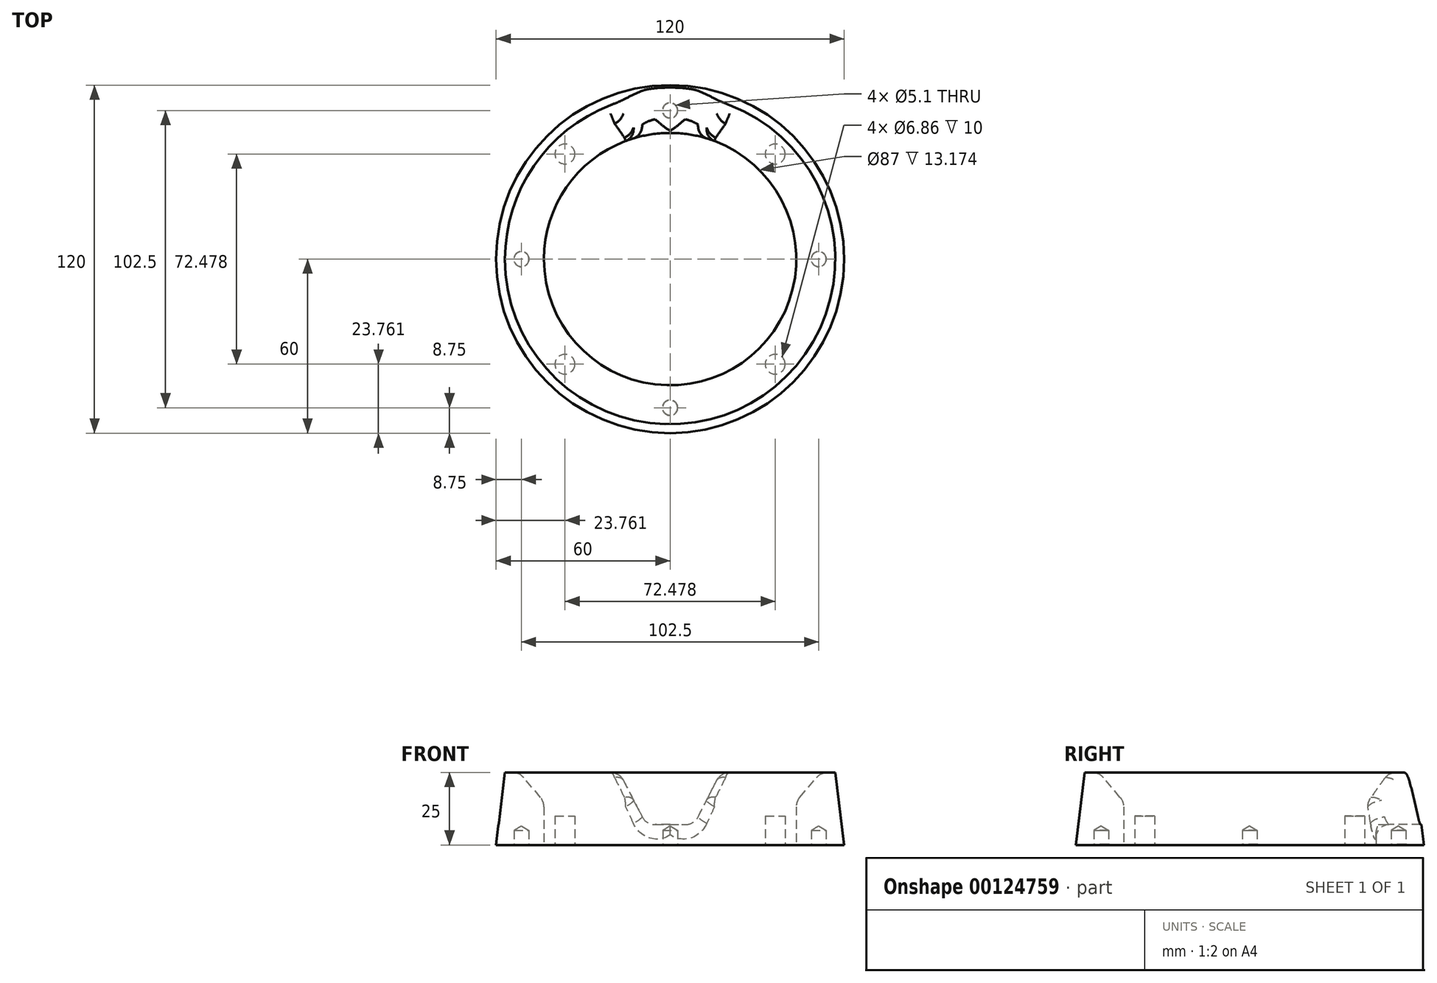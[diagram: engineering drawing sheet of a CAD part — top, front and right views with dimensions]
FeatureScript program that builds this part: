
annotation { "Feature Type Name" : "Feature", "Feature Type Description" : "" }
export const myFeature = defineFeature(function(context is Context, id is Id, definition is map)
    precondition{}
    {
        {
            var Q0;
            Q0=qCreatedBy(makeId("Front.planeOp"),FACE);
            var sketch = newSketch(context, id + "F0", { "sketchPlane" : qUnion([Q0])});
            skLineSegment(sketch, "E0", {"start": v(60, 0) * mm, "end": v(56.93, 25) * mm});
            skLineSegment(sketch, "E1", {"start": v(56.93, 25) * mm, "end": v(51.93, 25) * mm});
            skLineSegment(sketch, "E2", {"start": v(43.5, 0) * mm, "end": v(60, 0) * mm});
            skLineSegment(sketch, "E3", {"start": v(51.93, 25) * mm, "end": v(43.5, 15) * mm});
            skLineSegment(sketch, "E4", {"start": v(43.5, 15) * mm, "end": v(43.5, 0) * mm});
            skLineSegment(sketch, "E5", {"start": v(0, 0) * mm, "end": v(0, 25) * mm, "construction": true});
            skSolve(sketch);
        }
        {
            var Q0;
            Q0=makeQuery(id+"F0.imprint","IMPRINT",FACE,{"disambiguationData":[TD([[makeQuery(id+"F0.imprint","IMPRINT",EDGE,{"derivedFrom":sQuery(id+"F0.wireOp",EDGE,"E0")}),1.0]])]});
            var Q1;
            Q1=sQuery(id+"F0.wireOp",EDGE,"E5");
            revolve(context, id + "F1", {"entities" : qUnion([Q0]), "axis" : qUnion([Q1]), "revolveType" : RevolveType.FULL});
        }
        {
            var Q0;
            Q0=makeQuery(id+"F1.opRevolve","SWEPT_FACE",FACE,{"disambiguationData":[OSD([sQuery(id+"F0.wireOp",EDGE,"E2")])]});
            var sketch = newSketch(context, id + "F2", { "sketchPlane" : qUnion([Q0])});
            skCircle(sketch, "E6", {"center": v(0, 0) * mm, "radius": 51.25 * mm, "construction": true});
            skPoint(sketch, "E7", {"position": v(0, 51.25) * mm});
            skPoint(sketch, "E8", {"position": v(51.25, 0) * mm});
            skPoint(sketch, "E9", {"position": v(0, -51.25) * mm});
            skPoint(sketch, "E10", {"position": v(-51.25, 0) * mm});
            skPoint(sketch, "E11.1.0", {"position": v(36.24, 36.24) * mm});
            skPoint(sketch, "E11.1.1", {"position": v(36.24, -36.24) * mm});
            skPoint(sketch, "E11.1.2", {"position": v(-36.24, -36.24) * mm});
            skPoint(sketch, "E11.1.3", {"position": v(-36.24, 36.24) * mm});
            skLineSegment(sketch, "E11.anchor1", {"start": v(0, 0) * mm, "end": v(0, -51.25) * mm, "construction": true});
            skLineSegment(sketch, "E11.anchor2", {"start": v(0, 0) * mm, "end": v(-36.24, -36.24) * mm, "construction": true});
            skCircle(sketch, "E12", {"center": v(36.24, -36.24) * mm, "radius": 3.43 * mm});
            skCircle(sketch, "E13", {"center": v(-36.24, -36.24) * mm, "radius": 3.43 * mm});
            skCircle(sketch, "E14", {"center": v(-36.24, 36.24) * mm, "radius": 3.43 * mm});
            skCircle(sketch, "E15", {"center": v(36.24, 36.24) * mm, "radius": 3.43 * mm});
            skSolve(sketch);
        }
        {
            var Q0;
            Q0=sQuery(id+"F2.wireOp",VERTEX,"E7");
            var Q1;
            Q1=sQuery(id+"F2.wireOp",VERTEX,"E8");
            var Q2;
            Q2=sQuery(id+"F2.wireOp",VERTEX,"E9");
            var Q3;
            Q3=sQuery(id+"F2.wireOp",VERTEX,"E10");
            var Q4;
            Q4=makeQuery(id+"F1.opRevolve","SWEPT_BODY",BODY,{"disambiguationData":[OSD([sQuery(id+"F0.wireOp",EDGE,"E0"),sQuery(id+"F0.wireOp",EDGE,"E1"),sQuery(id+"F0.wireOp",EDGE,"E2"),sQuery(id+"F0.wireOp",EDGE,"E3"),sQuery(id+"F0.wireOp",EDGE,"E4")])]});
            hole(context, id + "F3", {"style" : HoleStyle.C_SINK, "endStyle" : HoleEndStyle.BLIND, "holeDiameter" : 5.1 * mm, "cSinkDiameter" : 5.3 * mm, "cSinkAngle" : 45 * degree, "holeDepth" : 5 * mm, "locations" : qUnion([Q0, Q1, Q2, Q3]), "scope" : qUnion([Q4])});
        }
        {
            var Q0;
            Q0=makeQuery(id+"F1.opRevolve","SWEPT_EDGE",EDGE,{"disambiguationData":[OSD([sQuery(id+"F0.wireOp",EDGE,"E1"),sQuery(id+"F0.wireOp",EDGE,"E3")])]});
            var Q1;
            Q1=makeQuery(id+"F1.opRevolve","SWEPT_EDGE",EDGE,{"disambiguationData":[OSD([sQuery(id+"F0.wireOp",EDGE,"E3"),sQuery(id+"F0.wireOp",EDGE,"E4")])]});
            fillet(context, id + "F4", {"entities" : qUnion([Q0, Q1]), "radius" : 5 * mm, "tangentPropagation" : true, "allowEdgeOverflow" : false});
        }
        {
            var Q0;
            Q0=qCreatedBy(makeId("Front.planeOp"),FACE);
            var sketch = newSketch(context, id + "F5", { "sketchPlane" : qUnion([Q0])});
            skLineSegment(sketch, "E16", {"start": v(-17.5, 25) * mm, "end": v(-8.25, 7) * mm});
            skLineSegment(sketch, "E17", {"start": v(-8.25, 7) * mm, "end": v(8.25, 7) * mm});
            skLineSegment(sketch, "E18", {"start": v(8.25, 7) * mm, "end": v(17.5, 25) * mm});
            skLineSegment(sketch, "E19", {"start": v(17.5, 25) * mm, "end": v(-17.5, 25) * mm});
            skPoint(sketch, "E20", {"position": v(0, 7) * mm});
            skSolve(sketch);
        }
        {
            var Q0;
            Q0 = qSketchRegion(id + "F5", true);
            extrude(context, id + "F6", {"entities" : qUnion([Q0]), "operationType" : NewBodyOperationType.REMOVE, "endBound" : BoundingType.THROUGH_ALL, "oppositeDirection" : true, "depth" : 25 * mm});
        }
        {
            var Q0;
            Q0=makeQuery(id+"F6.boolean.opBoolean","INTERSECT",EDGE,{"derivedFrom":[makeQuery(id+"F1.opRevolve","SWEPT_FACE",FACE,{"disambiguationData":[OSD([sQuery(id+"F0.wireOp",EDGE,"E3")])]}),makeQuery(id+"F6.opExtrude","SWEPT_FACE",FACE,{"disambiguationData":[OSD([sQuery(id+"F5.wireOp",EDGE,"E18")])]})]});
            var Q1;
            Q1=makeQuery(id+"F6.boolean.opBoolean","INTERSECT",EDGE,{"derivedFrom":[makeQuery(id+"F1.opRevolve","SWEPT_FACE",FACE,{"disambiguationData":[OSD([sQuery(id+"F0.wireOp",EDGE,"E3")])]}),makeQuery(id+"F6.opExtrude","SWEPT_FACE",FACE,{"disambiguationData":[OSD([sQuery(id+"F5.wireOp",EDGE,"E16")])]})]});
            var Q2;
            Q2=makeQuery(id+"F6.boolean.opBoolean","COPY",EDGE,{"derivedFrom":makeQuery(id+"F6.opExtrude","SWEPT_EDGE",EDGE,{"disambiguationData":[OSD([sQuery(id+"F5.wireOp",EDGE,"E17"),sQuery(id+"F5.wireOp",EDGE,"E18")])]})});
            var Q3;
            Q3=makeQuery(id+"F6.boolean.opBoolean","COPY",EDGE,{"derivedFrom":makeQuery(id+"F6.opExtrude","SWEPT_EDGE",EDGE,{"disambiguationData":[OSD([sQuery(id+"F5.wireOp",EDGE,"E16"),sQuery(id+"F5.wireOp",EDGE,"E17")])]})});
            fillet(context, id + "F7", {"entities" : qUnion([Q0, Q1, Q2, Q3]), "radius" : 5 * mm, "tangentPropagation" : true, "allowEdgeOverflow" : false});
        }
        {
            var Q0;
            Q0 = qSketchRegion(id + "F2", true);
            extrude(context, id + "F8", {"entities" : qUnion([Q0]), "operationType" : NewBodyOperationType.REMOVE, "oppositeDirection" : true, "depth" : 10 * mm});
        }
    });
